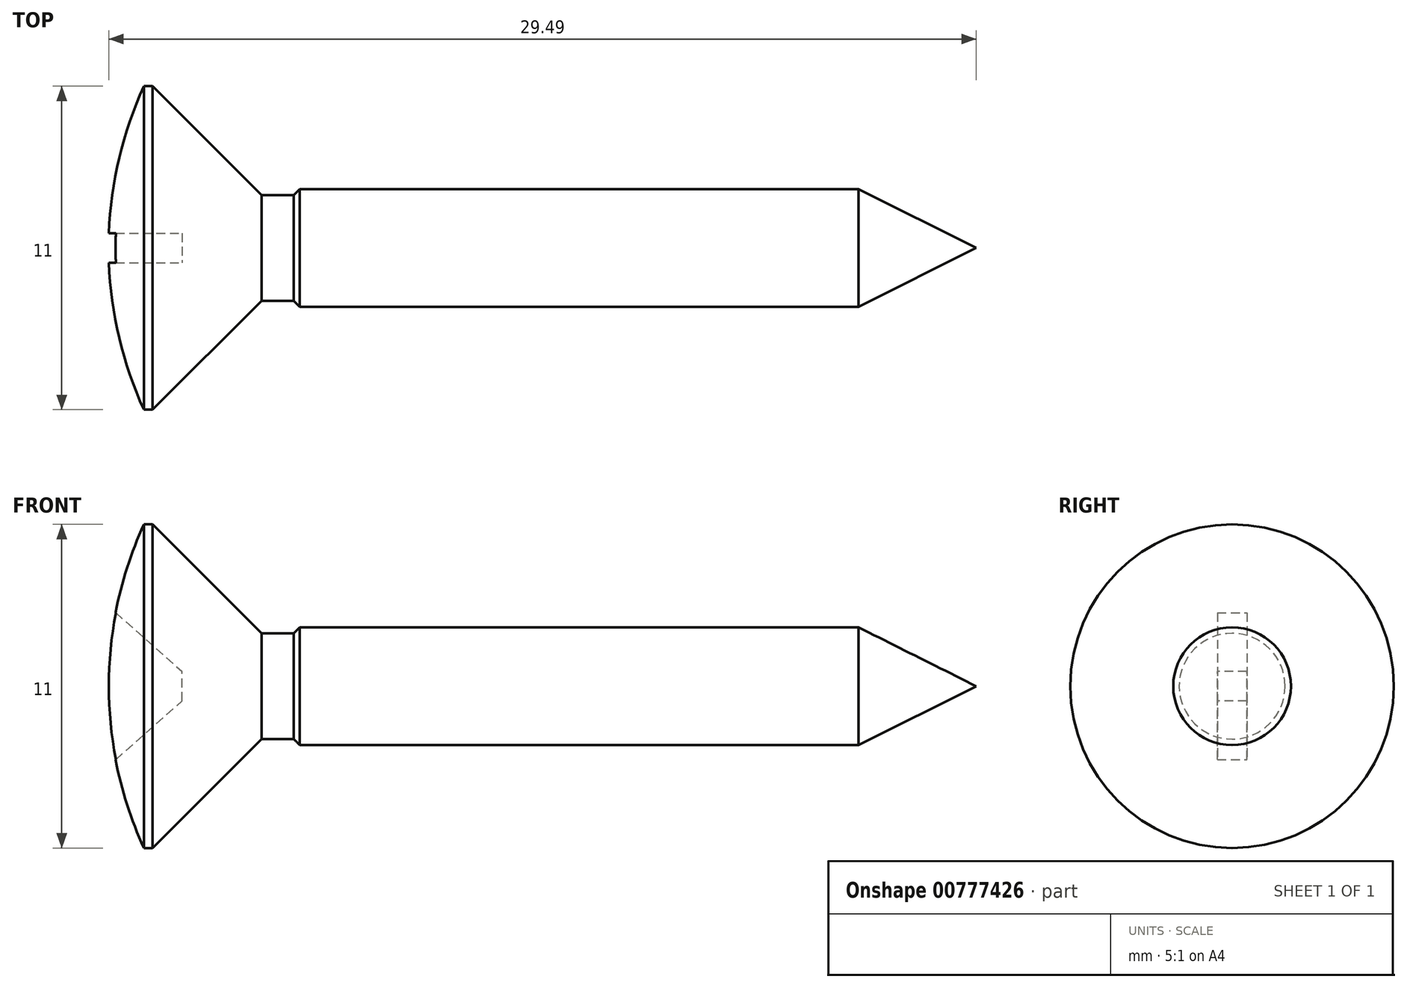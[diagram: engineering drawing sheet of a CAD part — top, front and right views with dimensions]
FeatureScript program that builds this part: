
annotation { "Feature Type Name" : "Feature", "Feature Type Description" : "" }
export const myFeature = defineFeature(function(context is Context, id is Id, definition is map)
    precondition{}
    {
        {
            var Q0;
            Q0=qCreatedBy(makeId("Front.planeOp"),FACE);
            var sketch = newSketch(context, id + "F0", { "sketchPlane" : qUnion([Q0])});
            skLineSegment(sketch, "E0", {"start": v(24, 2) * mm, "end": v(28, 0) * mm});
            skLineSegment(sketch, "E1", {"start": v(28, 0) * mm, "end": v(-1.5, 0) * mm});
            skLineSegment(sketch, "E2", {"start": v(-1.5, 0) * mm, "end": v(-1.5, 2.23) * mm, "construction": true});
            skLineSegment(sketch, "E3", {"start": v(-0.3, 5.5) * mm, "end": v(0, 5.5) * mm});
            skLineSegment(sketch, "E4", {"start": v(0, 5.5) * mm, "end": v(3.7, 1.8) * mm});
            skLineSegment(sketch, "E5", {"start": v(3.7, 1.8) * mm, "end": v(4.8, 1.8) * mm});
            skLineSegment(sketch, "E6", {"start": v(4.8, 1.8) * mm, "end": v(5, 2) * mm});
            skLineSegment(sketch, "E7", {"start": v(5, 2) * mm, "end": v(24, 2) * mm});
            skArc(sketch, "E8", {"start": v(-0.3, 5.5) * mm, "mid": v(-1.2, 2.81) * mm, "end": v(-1.5, 0) * mm});
            skSolve(sketch);
        }
        {
            var Q0;
            Q0=qSketchRegion(id+"F0",true);
            var Q1;
            Q1=sQuery(id+"F0.wireOp",EDGE,"E1");
            revolve(context, id + "F1", {"surfaceOperationType" : NewSurfaceOperationType.NEW, "entities" : qUnion([Q0]), "axis" : qUnion([Q1]), "revolveType" : RevolveType.FULL});
        }
        {
            var Q0;
            Q0=qCreatedBy(makeId("Front.planeOp"),FACE);
            var sketch = newSketch(context, id + "F2", { "sketchPlane" : qUnion([Q0])});
            skLineSegment(sketch, "E9", {"start": v(-1.5, 2.5) * mm, "end": v(-1.26, 2.5) * mm});
            skLineSegment(sketch, "E10", {"start": v(-1.26, 2.5) * mm, "end": v(1, 0.5) * mm});
            skLineSegment(sketch, "E11", {"start": v(1, 0.5) * mm, "end": v(1, 0) * mm});
            skLineSegment(sketch, "E12", {"start": v(-1.5, 2.5) * mm, "end": v(-1.5, 0) * mm});
            skLineSegment(sketch, "E13.MirrorCS", {"start": v(-1.5, -2.5) * mm, "end": v(-1.5, 0) * mm});
            skLineSegment(sketch, "E14.MirrorCS", {"start": v(-1.5, -2.5) * mm, "end": v(-1.26, -2.5) * mm});
            skLineSegment(sketch, "E15.MirrorCS", {"start": v(-1.26, -2.5) * mm, "end": v(1, -0.5) * mm});
            skLineSegment(sketch, "E16.MirrorCS", {"start": v(1, -0.5) * mm, "end": v(1, 0) * mm});
            skSolve(sketch);
        }
        {
            var Q0;
            Q0=qSketchRegion(id+"F2",true);
            extrude(context, id + "F3", {"entities" : qUnion([Q0]), "operationType" : NewBodyOperationType.REMOVE, "endBound" : BoundingType.SYMMETRIC, "oppositeDirection" : true, "depth" : 1 * mm, "offsetDistance" : 25 * mm});
        }
    });
